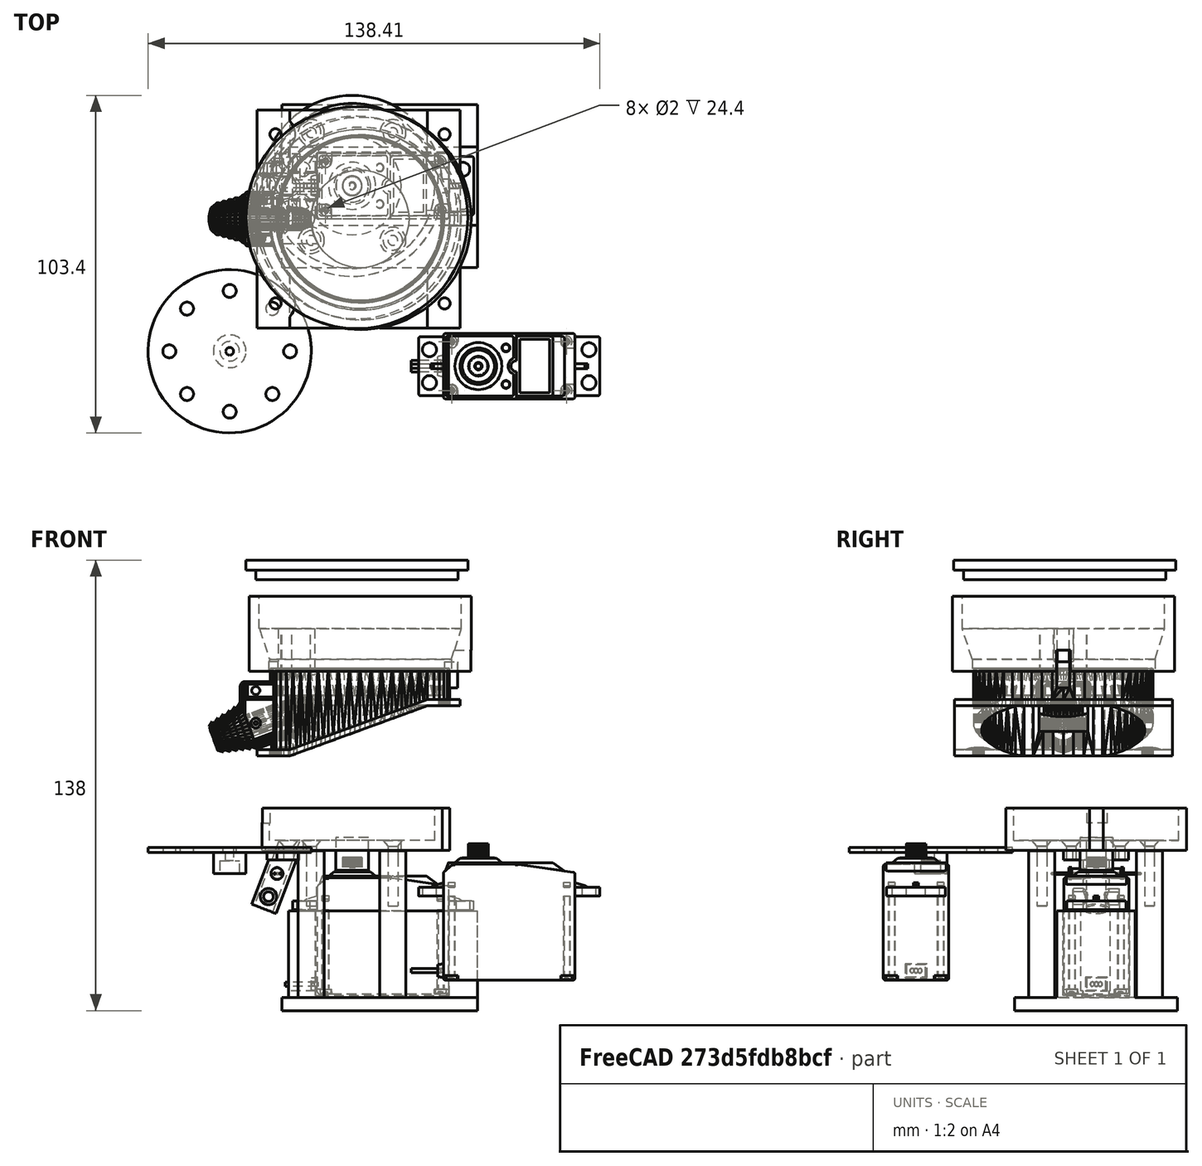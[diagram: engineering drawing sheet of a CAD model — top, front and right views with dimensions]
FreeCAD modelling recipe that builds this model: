
FCSTD DOCUMENT  (FreeCAD 0.21R33694 (Git))
Label: chute_with_mount_v2
License: All rights reserved
LicenseURL: http://en.wikipedia.org/wiki/All_rights_reserved
objects: Part::Cylinder×33, Part::Cut×23, Part::MultiFuse×20, Part::Feature×18, Part::Box×11, Part::FeaturePython×5, Sketcher::SketchObject×2, Part::Extrusion×2, Mesh::Feature×1, Part::Fillet×1, Part::Chamfer×1, Part::Cone×1
note: 117 computed .brp shape members not serialized (recipe doc carries the construction recipe); baked Part::Feature solids carry a one-line shape summary decoded from their .brp

FEATURE [Part::Box] Box014  label="Cube014"
  AttacherType = Attacher::AttachEngine3D
  Height = 13
  Length = 4.2
  Placement = pos=(66.2,37.3,63.6) rot=(0,0,1;0rad)
  Width = 4.2
FEATURE [Part::Cylinder] Cylinder022
  Angle = 360
  AttacherType = Attacher::AttachEngine3D
  FirstAngle = 0
  Height = 20
  Placement = pos=(15.5,39.3,51.5) rot=(0,1,0;0.366519rad)
  Radius = 3
  SecondAngle = 0
FEATURE [Part::Box] Box015  label="Cube015"
  AttacherType = Attacher::AttachEngine3D
  Height = 10
  Length = 10
  Placement = pos=(7,36.6,72) rot=(0,0,1;0rad)
  Width = 6.2
FEATURE [Mesh::Feature] Base_V7  label="Base V7"
FEATURE [Part::Feature] Base_V7001_solid  label="hopper (Solid)"
  shape: bbox 76.98 x 66.8 x 28.84 mm, 5900 faces (baked)
FEATURE [Part::Feature] Shape001
  Placement = pos=(47,50.7,-44.8) rot=(0,0,1;3.14159rad)
  shape: bbox 57.75 x 20 x 41.74 mm, 378 faces, 4 solids (baked)
FEATURE [Part::Cylinder] cylinder010  label="servo_central_shaft"
  Angle = 360
  AttacherType = Attacher::AttachEngine3D
  FirstAngle = 0
  Height = 10
  Placement = pos=(37.55,50.7,-7) rot=(0,0,1;0rad)
  Radius = 5
  SecondAngle = 0
FEATURE [Part::Box] Box  label="Cube"
  AttacherType = Attacher::AttachEngine3D
  Height = 27.5
  Length = 58
  Placement = pos=(18,38.6,-47) rot=(0,0,1;0rad)
  Width = 24
FEATURE [Part::Box] Box016  label="Cube016"
  AttacherType = Attacher::AttachEngine3D
  Height = 29.5
  Length = 53
  Placement = pos=(13,46,-44) rot=(0,0,1;0rad)
  Width = 9
FEATURE [Part::Cut] Cut
  Base = -> Box
  Tool = -> Box016
FEATURE [Part::Box] Box017  label="Cube017"
  AttacherType = Attacher::AttachEngine3D
  Height = 29.5
  Length = 10
  Placement = pos=(17,46.6,-46) rot=(0,0,1;0rad)
  Width = 8
FEATURE [Part::Cut] Cut019
  Base = -> Cut
  Tool = -> Box017
FEATURE [Part::Box] Box018  label="Cube018"
  AttacherType = Attacher::AttachEngine3D
  Height = 27.5
  Length = 41
  Placement = pos=(0.5,50.4,-44.2) rot=(0,0,1;0rad)
  Width = 20.4
FEATURE [Part::Fillet] Fillet
  Base = -> Box018
  Edges = 4 edges r=1: [Edge1,Edge3,Edge5,Edge7]
  Placement = pos=(25.85,-9.87885,-1.16822) rot=(0,0,1;0rad)
FEATURE [Part::Cut] Cut020
  Base = -> Cut019
  Tool = -> Fillet
FEATURE [Part::Box] Box020  label="base_plate"
  AttacherType = Attacher::AttachEngine3D
  Height = 4
  Length = 60
  Placement = pos=(16,25.6,-50) rot=(0,0,1;0rad)
  Width = 50
FEATURE [Part::Feature] BOLTS_part  label="Hex socket countersunk head screw M3 20.0"
  Placement = pos=(25,67,2.1) rot=(0,1,0;3.14159rad)
  shape: bbox 6 x 6 x 20 mm, 12 faces (baked)
FEATURE [Part::Feature] BOLTS_part001  label="Hex socket countersunk head screw M3 20.001"
  Placement = pos=(50,67,2.1) rot=(0,1,0;3.14159rad)
  shape: bbox 6 x 6 x 20 mm, 12 faces (baked)
FEATURE [Part::Feature] BOLTS_part002  label="Hex socket countersunk head screw M3 20.002"
  Placement = pos=(50,34,2.1) rot=(0,1,0;3.14159rad)
  shape: bbox 6 x 6 x 20 mm, 12 faces (baked)
FEATURE [Part::Feature] BOLTS_part003  label="Hex socket countersunk head screw M3 20.003"
  Placement = pos=(25,34,2.1) rot=(0,1,0;3.14159rad)
  shape: bbox 6 x 6 x 20 mm, 12 faces (baked)
FEATURE [Part::Cylinder] Cylinder024
  Angle = 360
  AttacherType = Attacher::AttachEngine3D
  FirstAngle = 0
  Height = 48
  Placement = pos=(50,67,-49) rot=(0,0,1;0rad)
  Radius = 4
  SecondAngle = 0
FEATURE [Part::Cylinder] Cylinder025
  Angle = 360
  AttacherType = Attacher::AttachEngine3D
  FirstAngle = 0
  Height = 48
  Placement = pos=(25,34,-49) rot=(0,0,1;0rad)
  Radius = 4
  SecondAngle = 0
FEATURE [Part::Cylinder] Cylinder026
  Angle = 360
  AttacherType = Attacher::AttachEngine3D
  FirstAngle = 0
  Height = 48
  Placement = pos=(25,67,-49) rot=(0,0,1;0rad)
  Radius = 4
  SecondAngle = 0
FEATURE [Part::Cylinder] Cylinder027
  Angle = 360
  AttacherType = Attacher::AttachEngine3D
  FirstAngle = 0
  Height = 48
  Placement = pos=(50,34,-49) rot=(0,0,1;0rad)
  Radius = 4
  SecondAngle = 0
FEATURE [Part::Feature] Shape002  label="led2"
  Placement = pos=(14.5,42.3,-8) rot=(-1,0,0;1.5708rad)
  shape: bbox 3.686 x 11.4 x 3.686 mm, 26 faces, 3 solids (baked)
FEATURE [Part::Feature] Shape003  label="led1"
  Placement = pos=(14.5,59.1,-8) rot=(1,0,0;1.5708rad)
  shape: bbox 3.686 x 11.4 x 3.686 mm, 26 faces, 3 solids (baked)
FEATURE [Part::Feature] BOLTS_part004  label="Hex socket countersunk head screw M3 20.004"
  Placement = pos=(25,34,2.05) rot=(0,1,0;3.14159rad)
  shape: bbox 6 x 6 x 20 mm, 12 faces (baked)
FEATURE [Part::Feature] BOLTS_part005  label="Hex socket countersunk head screw M3 20.005"
  Placement = pos=(50,34,2.05) rot=(0,1,0;3.14159rad)
  shape: bbox 6 x 6 x 20 mm, 12 faces (baked)
FEATURE [Part::Feature] BOLTS_part006  label="Hex socket countersunk head screw M3 20.006"
  Placement = pos=(50,67,2.05) rot=(0,1,0;3.14159rad)
  shape: bbox 6 x 6 x 20 mm, 12 faces (baked)
FEATURE [Part::Feature] BOLTS_part007  label="Hex socket countersunk head screw M3 20.007"
  Placement = pos=(25,67,2.05) rot=(0,1,0;3.14159rad)
  shape: bbox 6 x 6 x 20 mm, 12 faces (baked)
FEATURE [Part::Cylinder] Cylinder032
  Angle = 360
  AttacherType = Attacher::AttachEngine3D
  FirstAngle = 0
  Height = 48
  Placement = pos=(50,67,-43) rot=(0,0,1;0rad)
  Radius = 1.4
  SecondAngle = 0
FEATURE [Part::Cylinder] Cylinder033
  Angle = 360
  AttacherType = Attacher::AttachEngine3D
  FirstAngle = 0
  Height = 48
  Placement = pos=(25,34,-43) rot=(0,0,1;0rad)
  Radius = 1.4
  SecondAngle = 0
FEATURE [Part::Cylinder] Cylinder034
  Angle = 360
  AttacherType = Attacher::AttachEngine3D
  FirstAngle = 0
  Height = 48
  Placement = pos=(25,67,-42) rot=(0,0,1;0rad)
  Radius = 1.4
  SecondAngle = 0
FEATURE [Part::Cylinder] Cylinder035
  Angle = 360
  AttacherType = Attacher::AttachEngine3D
  FirstAngle = 0
  Height = 48
  Placement = pos=(50,34,-43) rot=(0,0,1;0rad)
  Radius = 1.4
  SecondAngle = 0
FEATURE [Part::Cut] Cut030
  Base = -> Cylinder024
  Tool = -> BOLTS_part006
FEATURE [Part::Cut] Cut031
  Base = -> Cylinder025
  Tool = -> BOLTS_part004
FEATURE [Part::Cut] Cut032
  Base = -> Cylinder026
  Tool = -> BOLTS_part007
FEATURE [Part::Cut] Cut033
  Base = -> Cylinder027
  Tool = -> BOLTS_part005
FEATURE [Part::MultiFuse] Fusion011  label="motor_holder"
  Shapes = -> [Cut020,Cut030,Cut031,Cut032,Cut033,Box020]
FEATURE [Part::Cylinder] Cylinder039
  Angle = 360
  AttacherType = Attacher::AttachEngine3D
  FirstAngle = 0
  Height = 21
  Placement = pos=(0,10,4) rot=(1,0,0;1.5708rad)
  Radius = 1.5
  SecondAngle = 0
FEATURE [Part::FeaturePython] Tube003  # WARN: FeaturePython — macro-defined, semantics opaque (R4)
  AttacherType = Attacher::AttachEngine3D
  Height = 5
  InnerRadius = 1.5
  OuterRadius = 2.5
  Placement = pos=(0,2.05,4) rot=(-1,0,0;1.5708rad)
FEATURE [Part::FeaturePython] Tube004  # WARN: FeaturePython — macro-defined, semantics opaque (R4)
  AttacherType = Attacher::AttachEngine3D
  Height = 5
  InnerRadius = 1.5
  OuterRadius = 2.5
  Placement = pos=(0,-2.05,4) rot=(1,0,0;1.5708rad)
FEATURE [Part::Box] Box021  label="Cube019"
  AttacherType = Attacher::AttachEngine3D
  Height = 10
  Length = 20
  Placement = pos=(1.17,-11.94,17.9) rot=(0,0,1;0rad)
  Width = 24
FEATURE [Part::FeaturePython] Tube001  # WARN: FeaturePython — macro-defined, semantics opaque (R4)
  AttacherType = Attacher::AttachEngine3D
  Height = 3
  InnerRadius = 15
  OuterRadius = 27.7
  Placement = pos=(40.45,39.4,63.6) rot=(0,0,1;0rad)
FEATURE [Part::FeaturePython] Tube002  # WARN: FeaturePython — macro-defined, semantics opaque (R4)
  AttacherType = Attacher::AttachEngine3D
  Height = 13
  InnerRadius = 25.3
  OuterRadius = 27.7
  Placement = pos=(40.45,39.4,63.6) rot=(0,0,1;0rad)
FEATURE [Part::MultiFuse] Fusion009
  Shapes = -> [Box014,Tube001,Tube002]
FEATURE [Part::Cut] Cut014  label="cut"
  Base = -> Fusion009
  Tool = -> Cylinder022
FEATURE [Part::Cut] Cut036
  Base = -> Cut014
  Placement = pos=(-2.9,11.3,-64.5) rot=(0,0,1;0rad)
  Tool = -> Box015
FEATURE [Part::MultiFuse] Fusion
  Shapes = -> [BOLTS_part003,Cylinder033]
FEATURE [Part::MultiFuse] Fusion013
  Shapes = -> [BOLTS_part002,Cylinder035]
FEATURE [Part::MultiFuse] Fusion014
  Shapes = -> [BOLTS_part001,Cylinder032]
FEATURE [Part::MultiFuse] Fusion015
  Shapes = -> [BOLTS_part,Cylinder034]
FEATURE [Part::Cut] Cut037
  Base = -> Cut036
  Tool = -> Fusion
FEATURE [Part::Cut] Cut038
  Base = -> Cut037
  Tool = -> Fusion013
FEATURE [Part::Cut] Cut039
  Base = -> Cut038
  Tool = -> Fusion015
FEATURE [Part::Cut] Cut040
  Base = -> Cut039
  Tool = -> Fusion014
FEATURE [Part::Feature] BOLTS_part009  label="Hex socket countersunk head screw M3 20.008"
  Placement = pos=(50,34,2.1) rot=(0,1,0;3.14159rad)
  shape: bbox 6 x 6 x 20 mm, 12 faces (baked)
FEATURE [Part::Cylinder] Cylinder040
  Angle = 360
  AttacherType = Attacher::AttachEngine3D
  FirstAngle = 0
  Height = 48
  Placement = pos=(50,34,-43) rot=(0,0,1;0rad)
  Radius = 1.4
  SecondAngle = 0
FEATURE [Part::MultiFuse] Fusion016
  Placement = pos=(-32,9,0) rot=(0,0,1;0rad)
  Shapes = -> [BOLTS_part009,Cylinder040]
FEATURE [Part::Feature] BOLTS_part010  label="Hex socket countersunk head screw M3 20.009"
  Placement = pos=(50,34,2.1) rot=(0,1,0;3.14159rad)
  shape: bbox 6 x 6 x 20 mm, 12 faces (baked)
FEATURE [Part::Cylinder] Cylinder041
  Angle = 360
  AttacherType = Attacher::AttachEngine3D
  FirstAngle = 0
  Height = 48
  Placement = pos=(50,34,-43) rot=(0,0,1;0rad)
  Radius = 1.4
  SecondAngle = 0
FEATURE [Part::MultiFuse] Fusion017
  Placement = pos=(-32,24,0) rot=(0,0,1;0rad)
  Shapes = -> [BOLTS_part010,Cylinder041]
FEATURE [Part::Box] Box022  label="Cube020"
  AttacherType = Attacher::AttachEngine3D
  Height = 3
  Length = 10
  Placement = pos=(3,-10,15) rot=(0,0,1;0rad)
  Width = 20
FEATURE [Part::Cylinder] Cylinder
  Angle = 360
  AttacherType = Attacher::AttachEngine3D
  FirstAngle = 0
  Height = 18
  Radius = 4
  SecondAngle = 0
FEATURE [Part::Cylinder] Cylinder043
  Angle = 360
  AttacherType = Attacher::AttachEngine3D
  FirstAngle = 0
  Height = 50
  Placement = pos=(0,0,-5) rot=(0,1,0;0.366519rad)
  Radius = 3
  SecondAngle = 0
FEATURE [Part::Cut] Cut043
  Base = -> Cylinder
  Tool = -> Cylinder039
FEATURE [Part::MultiFuse] Fusion018
  Placement = pos=(2,0,0) rot=(0,1,0;0.366519rad)
  Shapes = -> [Tube003,Tube004,Cut043]
FEATURE [Part::MultiFuse] Fusion019
  Shapes = -> [Fusion018,Box022]
FEATURE [Part::MultiFuse] Fusion020
  Shapes = -> [Cylinder043,Box021]
FEATURE [Part::Cut] Cut044  label="foodchute"
  Base = -> Fusion019
  Placement = pos=(8.45427,50.6,-18.8) rot=(0,0,1;0rad)
  Tool = -> Fusion020
FEATURE [Part::Chamfer] Chamfer
  Base = -> Cut044
  Edges = 2 edges r=3: [Edge1,Edge3]
FEATURE [Part::Feature] BOLTS_part011  label="Hex socket countersunk head screw M3 20.010"
  Placement = pos=(50,34,2.1) rot=(0,1,0;3.14159rad)
  shape: bbox 6 x 6 x 20 mm, 12 faces (baked)
FEATURE [Part::Cylinder] Cylinder044
  Angle = 360
  AttacherType = Attacher::AttachEngine3D
  FirstAngle = 0
  Height = 48
  Placement = pos=(50,34,-43) rot=(0,0,1;0rad)
  Radius = 1.4
  SecondAngle = 0
FEATURE [Part::MultiFuse] Fusion021
  Placement = pos=(-32,9,0) rot=(0,0,1;0rad)
  Shapes = -> [BOLTS_part011,Cylinder044]
FEATURE [Part::Feature] BOLTS_part012  label="Hex socket countersunk head screw M3 20.011"
  Placement = pos=(50,34,2.1) rot=(0,1,0;3.14159rad)
  shape: bbox 6 x 6 x 20 mm, 12 faces (baked)
FEATURE [Part::Cylinder] Cylinder045
  Angle = 360
  AttacherType = Attacher::AttachEngine3D
  FirstAngle = 0
  Height = 48
  Placement = pos=(50,34,-43) rot=(0,0,1;0rad)
  Radius = 1.4
  SecondAngle = 0
FEATURE [Part::MultiFuse] Fusion022
  Placement = pos=(-32,24,0) rot=(0,0,1;0rad)
  Shapes = -> [BOLTS_part012,Cylinder045]
FEATURE [Part::Cut] Cut045
  Base = -> Chamfer
  Tool = -> Fusion021
FEATURE [Part::Cut] Cut046  label="chute_with_mount"
  Base = -> Cut045
  Tool = -> Fusion022
FEATURE [Part::Cut] Cut047
  Base = -> Cut040
  Tool = -> Fusion016
FEATURE [Part::Cut] Cut048  label="base"
  Base = -> Cut047
  Tool = -> Fusion017
FEATURE [Part::Feature] Shape004
  Placement = pos=(85.6641,-4.55315,-40.6487) rot=(0,0,1;3.14159rad)
  shape: bbox 57.75 x 20 x 41.74 mm, 378 faces, 4 solids (baked)
FEATURE [Part::Box] Box012  label="Cube012"
  AttacherType = Attacher::AttachEngine3D
  Height = 10
  Length = 10
  Placement = pos=(7,36.17,76) rot=(0,0,1;0rad)
  Width = 6
FEATURE [Part::Box] Box013  label="Cube013"
  AttacherType = Attacher::AttachEngine3D
  Height = 10
  Length = 14
  Placement = pos=(64,38.5,50.5) rot=(0,0,1;0rad)
  Width = 4.3
FEATURE [Part::Cone] Cone
  Angle = 360
  AttacherType = Attacher::AttachEngine3D
  Height = 14
  Placement = pos=(40,40.65,53) rot=(0,0,1;0rad)
  Radius1 = 26.5
  Radius2 = 31
FEATURE [Part::Cylinder] Cylinder019
  Angle = 360
  AttacherType = Attacher::AttachEngine3D
  FirstAngle = 0
  Height = 13
  Placement = pos=(40,40.65,54) rot=(0,0,1;0rad)
  Radius = 34
  SecondAngle = 0
FEATURE [Part::Cylinder] Cylinder020
  Angle = 360
  AttacherType = Attacher::AttachEngine3D
  FirstAngle = 0
  Height = 13
  Placement = pos=(40,39.2,54) rot=(0,0,1;0rad)
  Radius = 25
  SecondAngle = 0
FEATURE [Part::Cylinder] Cylinder021
  Angle = 360
  AttacherType = Attacher::AttachEngine3D
  FirstAngle = 0
  Height = 4
  Placement = pos=(40,40.65,54) rot=(0,0,1;0rad)
  Radius = 28
  SecondAngle = 0
FEATURE [Sketcher::SketchObject] Sketch001
  FullyConstrained = true
  MapMode = 2
  Placement = pos=(0,5,65) rot=(0,0,1;0rad)
  sketch-geometry (8):
    g0: ArcOfCircle CenterX=20.555 CenterY=41.4363 CenterZ=0 NormalX=0 NormalY=0 NormalZ=1 AngleXU=0 Radius=4.5 StartAngle=3.17145 EndAngle=4.38602
    g1: ArcOfCircle CenterX=24.0176 CenterY=34.022 CenterZ=0 NormalX=0 NormalY=0 NormalZ=1 AngleXU=0 Radius=2 StartAngle=5.10518 EndAngle=7.46119
    g2: ArcOfCircle CenterX=20.5312 CenterY=26.882 CenterZ=0 NormalX=0 NormalY=0 NormalZ=1 AngleXU=0 Radius=4.5 StartAngle=1.8916 EndAngle=3.11914
    g3: LineSegment StartX=19.1123 StartY=31.1525 StartZ=0 EndX=24.7831 EndY=32.1743 EndZ=0
    g4: LineSegment StartX=19.1123 StartY=37.1738 StartZ=0 EndX=24.7831 EndY=35.8697 EndZ=0
    g5: LineSegment StartX=16.057 StartY=41.302 StartZ=0 EndX=15.8089 EndY=41.3763 EndZ=0
    g6: LineSegment StartX=15.8133 StartY=26.9187 StartZ=0 EndX=16.0324 EndY=26.9831 EndZ=0
    g7: ArcOfCircle CenterX=39.7432 CenterY=34.1548 CenterZ=0 NormalX=0 NormalY=0 NormalZ=1 AngleXU=0 Radius=25 StartAngle=2.84856 EndAngle=3.43524
  constraints (28):
    c: Coincident(g3,g2)
    c: Coincident(g3,g1)
    c: Coincident(g4,g0)
    c: Coincident(g4,g1)
    c: Coincident(g5,g0)
    c: Coincident(g6,g2)
    c: Coincident(g7,g6)
    c: Coincident(g7,g5)
    c: Radius(g2) = 4.5
    c: Radius(g0) = 4.5
    c: Radius(g1) = 2
    c: Radius(g7) = 25
    c: DistanceX(g5) = 15.8089
    c: DistanceY(g5) = 41.3763
    c: DistanceX(g2) = 16.0324
    c: DistanceY(g2) = 26.9831
    c: DistanceX(g3) = 19.1123
    c: DistanceY(g3) = 31.1525
    c: DistanceX(g2,g0) = 0
    c: DistanceX(g3,g1) = 0
    c: DistanceX(g1) = 24.7831
    c: DistanceY(g1) = 32.1743
    c: DistanceX(g5) = 16.057
    c: DistanceY(g5) = 41.302
    c: DistanceX(g7) = 15.8133
    c: DistanceY(g7) = 26.9187
    c: DistanceY(g1) = 35.8697
    c: DistanceY(g0) = 37.1738
FEATURE [Part::Extrusion] Extrude001
  Base = -> Sketch001
  Dir = (0,0,1)
  DirMode = 2
  FaceMakerClass = Part::FaceMakerBullseye
  LengthFwd = 14
  LengthRev = 0
  Placement = pos=(0,0,7) rot=(0,0,1;0rad)
  Solid = true
  Symmetric = false
FEATURE [Part::MultiFuse] Fusion006  label="pellet_sorter"
  Placement = pos=(0,1.5,-19) rot=(0,0,1;0rad)
  Shapes = -> [Box012,Extrude001]
FEATURE [Part::FeaturePython] Tube  # WARN: FeaturePython — macro-defined, semantics opaque (R4)
  AttacherType = Attacher::AttachEngine3D
  Height = 23
  InnerRadius = 31
  OuterRadius = 34
  Placement = pos=(40,40.65,54) rot=(0,0,1;0rad)
FEATURE [Part::MultiFuse] Fusion010
  Shapes = -> [Tube,Cylinder019,Cylinder020]
FEATURE [Part::Cut] Cut015
  Base = -> Fusion010
  Tool = -> Cone
FEATURE [Part::Cut] Cut016
  Base = -> Cut015
  Tool = -> Cylinder021
FEATURE [Part::MultiFuse] Fusion024
  Shapes = -> [Fusion006,Cut016]
FEATURE [Part::Cut] Cut017  label="lid"
  Base = -> Fusion024
  Tool = -> Box013
FEATURE [Part::Cylinder] Cylinder047
  Angle = 360
  AttacherType = Attacher::AttachEngine3D
  FirstAngle = 0
  Height = 3
  Radius = 34
  SecondAngle = 0
FEATURE [Part::Cylinder] Cylinder048
  Angle = 360
  AttacherType = Attacher::AttachEngine3D
  FirstAngle = 0
  Height = 6
  Radius = 31
  SecondAngle = 0
FEATURE [Part::MultiFuse] Fusion025  label="cap"
  Placement = pos=(39,41,88) rot=(1,0,0;3.14159rad)
  Shapes = -> [Cylinder047,Cylinder048]
FEATURE [Part::Cylinder] cylinder012
  Angle = 360
  AttacherType = Attacher::AttachEngine3D
  FirstAngle = 0
  Height = 1.5
  Radius = 25
  SecondAngle = 0
FEATURE [Part::Cylinder] cylinder013
  Angle = 360
  AttacherType = Attacher::AttachEngine3D
  FirstAngle = 0
  Height = 5
  Placement = pos=(18.5,0,0) rot=(0,0,1;0rad)
  Radius = 2
  SecondAngle = 0
FEATURE [Part::Cylinder] cylinder014
  Angle = 360
  AttacherType = Attacher::AttachEngine3D
  FirstAngle = 0
  Height = 5
  Placement = pos=(13.0815,13.0815,0) rot=(0,0,1;0.785398rad)
  Radius = 2
  SecondAngle = 0
FEATURE [Part::Cylinder] cylinder015
  Angle = 360
  AttacherType = Attacher::AttachEngine3D
  FirstAngle = 0
  Height = 5
  Placement = pos=(0,18.5,0) rot=(0,0,1;1.5708rad)
  Radius = 2
  SecondAngle = 0
FEATURE [Part::Cylinder] cylinder016
  Angle = 360
  AttacherType = Attacher::AttachEngine3D
  FirstAngle = 0
  Height = 5
  Placement = pos=(-13.0815,13.0815,0) rot=(0,0,1;2.35619rad)
  Radius = 2
  SecondAngle = 0
FEATURE [Part::Cylinder] cylinder017
  Angle = 360
  AttacherType = Attacher::AttachEngine3D
  FirstAngle = 0
  Height = 5
  Placement = pos=(-18.5,2e-15,0) rot=(0,0,1;3.14159rad)
  Radius = 2
  SecondAngle = 0
FEATURE [Part::Cylinder] cylinder018
  Angle = 360
  AttacherType = Attacher::AttachEngine3D
  FirstAngle = 0
  Height = 5
  Placement = pos=(-13.0815,-13.0815,0) rot=(0,0,1;3.92699rad)
  Radius = 2
  SecondAngle = 0
FEATURE [Part::Cylinder] cylinder019
  Angle = 360
  AttacherType = Attacher::AttachEngine3D
  FirstAngle = 0
  Height = 5
  Placement = pos=(0,-18.5,0) rot=(0,0,-1;1.5708rad)
  Radius = 2
  SecondAngle = 0
FEATURE [Part::Cylinder] cylinder020
  Angle = 360
  AttacherType = Attacher::AttachEngine3D
  FirstAngle = 0
  Height = 5
  Placement = pos=(13.0815,-13.0815,0) rot=(0,0,-1;0.785398rad)
  Radius = 2
  SecondAngle = 0
FEATURE [Part::MultiFuse] Group001
  Placement = pos=(0,0,-1) rot=(0,0,1;0rad)
  Shapes = -> [cylinder013,cylinder014,cylinder015,cylinder016,cylinder017,cylinder018,cylinder019,cylinder020]
FEATURE [Part::Feature] Shape005
  Placement = pos=(85.6641,-4.55315,-40.6487) rot=(0,0,1;3.14159rad)
  shape: bbox 57.75 x 20 x 41.74 mm, 378 faces, 4 solids (baked)
FEATURE [Part::Cylinder] cylinder021  label="servo_central_shaft002"
  Angle = 360
  AttacherType = Attacher::AttachEngine3D
  FirstAngle = 0
  Height = 8
  Radius = 5
  SecondAngle = 0
FEATURE [Sketcher::SketchObject] Sketch002
  FullyConstrained = false
  MapMode = 5
  Placement = pos=(85.6641,-4.55315,1.09128) rot=(0,0,1;3.14159rad)
  Support = -> [Shape005]
  sketch-geometry (1):
    g0: Circle CenterX=9.4502 CenterY=-0.000218 CenterZ=0 NormalX=0 NormalY=0 NormalZ=1 AngleXU=0 Radius=3
  constraints (1):
    c: Radius(g0) = 3
FEATURE [Part::Extrusion] Extrude002
  Base = -> Sketch002
  Dir = (0,0,1)
  DirMode = 2
  FaceMakerClass = Part::FaceMakerBullseye
  LengthFwd = 6
  LengthRev = 0
  Placement = pos=(-76.21,4.55,3) rot=(0,0,1;0rad)
  Solid = true
  Symmetric = false
FEATURE [Part::Cylinder] Cylinder049
  Angle = 360
  AttacherType = Attacher::AttachEngine3D
  FirstAngle = 0
  Height = 19
  Placement = pos=(0,0,-1) rot=(0,0,1;0rad)
  Radius = 1.2
  SecondAngle = 0
FEATURE [Part::MultiFuse] Fusion026
  Shapes = -> [Group001,Extrude002,Cylinder049]
FEATURE [Part::MultiFuse] Fusion027
  Shapes = -> [cylinder012,cylinder021]
FEATURE [Part::Cut] Cut050  label="rotor001"
  Base = -> Fusion027
  Placement = pos=(0,0,0) rot=(1,0,0;3.14159rad)
  Tool = -> Fusion026
